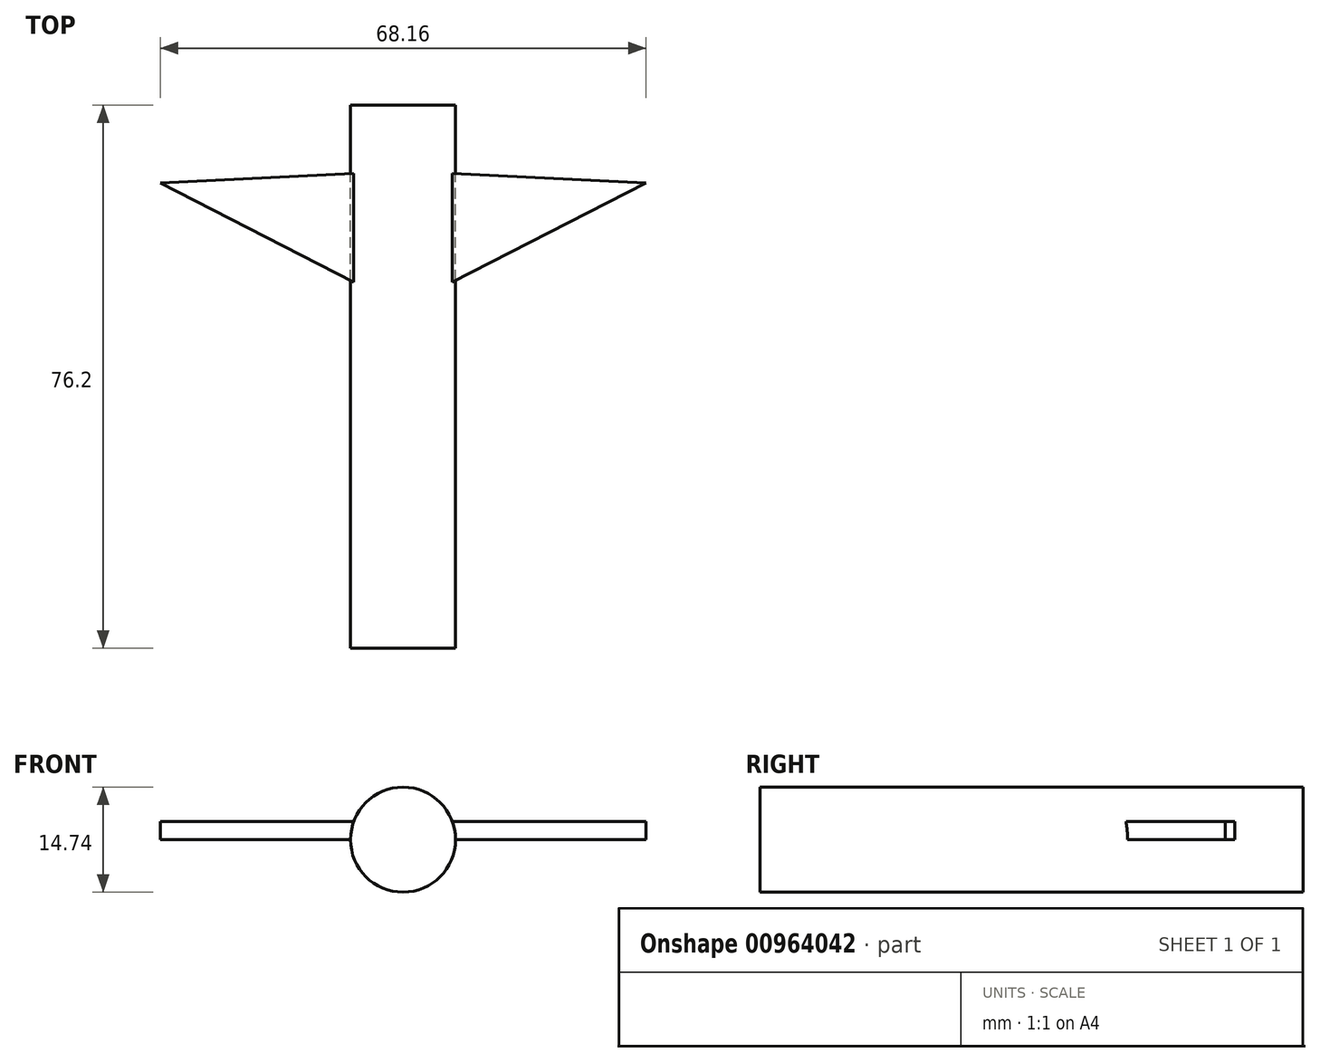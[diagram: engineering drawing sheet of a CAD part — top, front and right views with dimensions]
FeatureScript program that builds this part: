
annotation { "Feature Type Name" : "Feature", "Feature Type Description" : "" }
export const myFeature = defineFeature(function(context is Context, id is Id, definition is map)
    precondition{}
    {
        {
            var Q0;
            Q0=qCreatedBy(makeId("Front.planeOp"),FACE);
            var sketch = newSketch(context, id + "F0", { "sketchPlane" : qUnion([Q0])});
            skCircle(sketch, "E0", {"center": v(0, 0) * mm, "radius": 7.37 * mm});
            skSolve(sketch);
        }
        {
            var Q0;
            Q0=makeQuery(id+"F0.imprint","IMPRINT",FACE,{"disambiguationData":[TD([[makeQuery(id+"F0.imprint","IMPRINT",EDGE,{"derivedFrom":sQuery(id+"F0.wireOp",EDGE,"E0")}),1.0]])]});
            extrude(context, id + "F1", {"entities" : qUnion([Q0]), "endBound" : BoundingType.SYMMETRIC, "depth" : 76.2 * mm, "offsetDistance" : 25.4 * mm});
        }
        {
            var Q0;
            Q0=qCreatedBy(makeId("Top.planeOp"),FACE);
            var sketch = newSketch(context, id + "F2", { "sketchPlane" : qUnion([Q0])});
            skLineSegment(sketch, "E1", {"start": v(0, 9.7) * mm, "end": v(34.08, 27.2) * mm});
            skLineSegment(sketch, "E2", {"start": v(34.08, 27.2) * mm, "end": v(0, 28.87) * mm});
            skLineSegment(sketch, "E3.MirrorCS", {"start": v(0, 9.7) * mm, "end": v(-34.08, 27.2) * mm});
            skLineSegment(sketch, "E4.MirrorCS", {"start": v(-34.08, 27.2) * mm, "end": v(0, 28.87) * mm});
            skSolve(sketch);
        }
        {
            var Q0;
            Q0=makeQuery(id+"F2.imprint","IMPRINT",FACE,{"disambiguationData":[TD([[makeQuery(id+"F2.imprint","IMPRINT",EDGE,{"derivedFrom":sQuery(id+"F2.wireOp",EDGE,"E1")}),1.0]])]});
            extrude(context, id + "F3", {"entities" : qUnion([Q0]), "operationType" : NewBodyOperationType.ADD, "depth" : 2.54 * mm, "offsetDistance" : 25.4 * mm});
        }
    });
